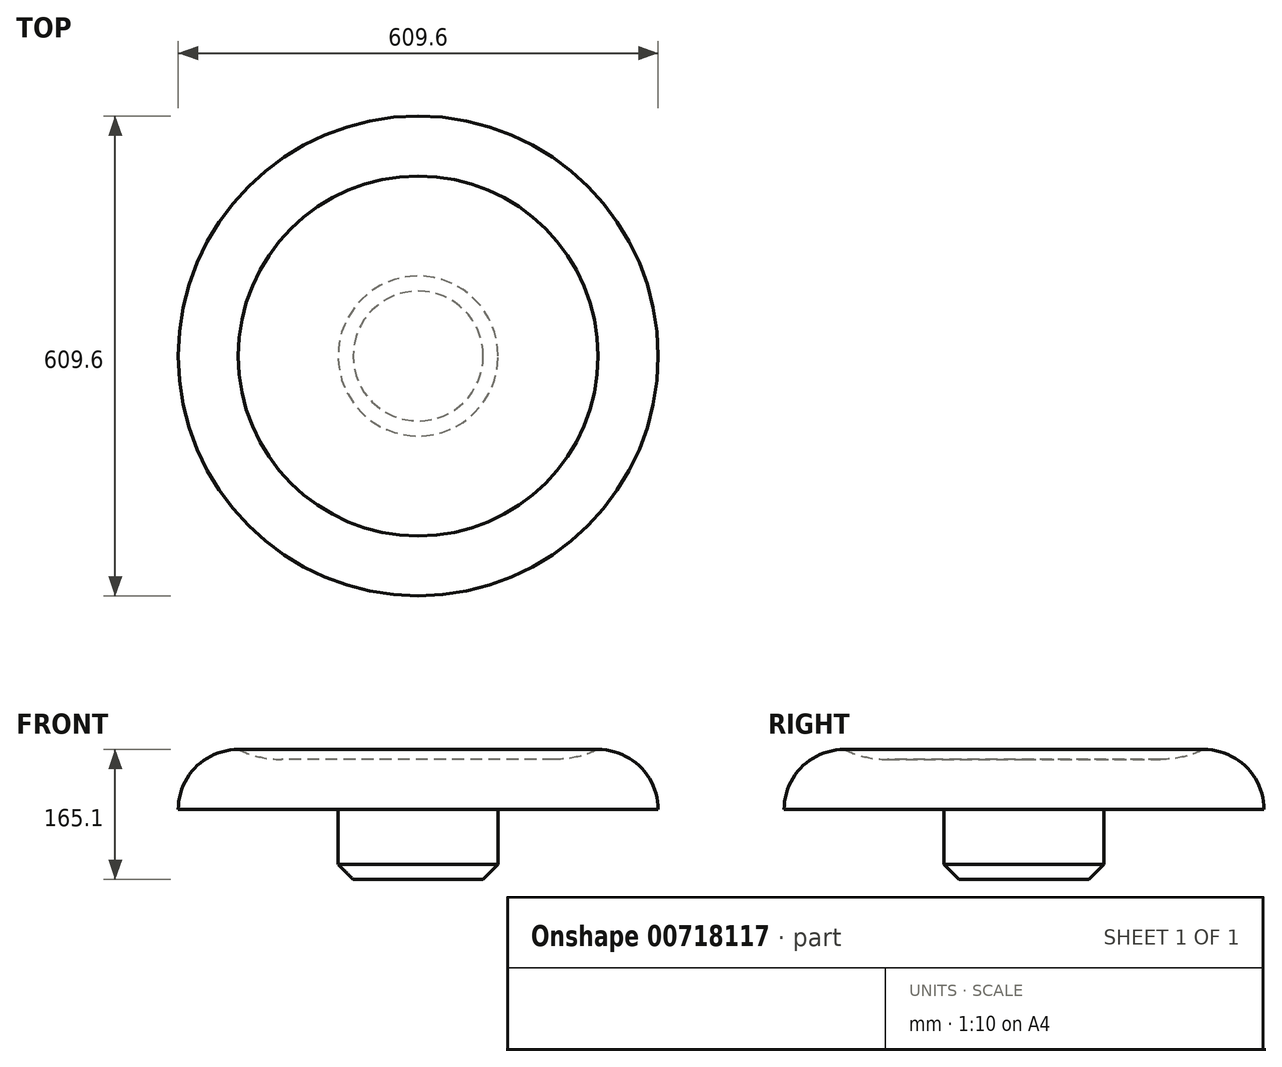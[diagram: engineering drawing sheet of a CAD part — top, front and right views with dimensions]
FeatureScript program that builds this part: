
annotation { "Feature Type Name" : "Feature", "Feature Type Description" : "" }
export const myFeature = defineFeature(function(context is Context, id is Id, definition is map)
    precondition{}
    {
        {
            var Q0;
            Q0=qCreatedBy(makeId("Top.planeOp"),FACE);
            var sketch = newSketch(context, id + "F0", { "sketchPlane" : qUnion([Q0])});
            skCircle(sketch, "E0", {"center": v(0, 0) * mm, "radius": 304.8 * mm});
            skSolve(sketch);
        }
        {
            var Q0;
            Q0=makeQuery(id+"F0.imprint","IMPRINT",FACE,{"disambiguationData":[TD([[makeQuery(id+"F0.imprint","IMPRINT",EDGE,{"derivedFrom":sQuery(id+"F0.wireOp",EDGE,"E0")}),1.0]])]});
            extrude(context, id + "F1", {"entities" : qUnion([Q0]), "depth" : 76.2 * mm, "offsetDistance" : 25.4 * mm});
        }
        {
            var Q0;
            Q0=makeQuery(id+"F1.opExtrude","CAP_FACE",FACE,{"disambiguationData":[OSD([sQuery(id+"F0.wireOp",EDGE,"E0")])],"isStart":true});
            var sketch = newSketch(context, id + "F2", { "sketchPlane" : qUnion([Q0])});
            skCircle(sketch, "E1", {"center": v(0, 0) * mm, "radius": 101.6 * mm});
            skSolve(sketch);
        }
        {
            var Q0;
            Q0=makeQuery(id+"F2.imprint","IMPRINT",FACE,{"disambiguationData":[TD([[makeQuery(id+"F2.imprint","IMPRINT",EDGE,{"derivedFrom":sQuery(id+"F2.wireOp",EDGE,"E1")}),1.0]])]});
            extrude(context, id + "F3", {"entities" : qUnion([Q0]), "operationType" : NewBodyOperationType.ADD, "depth" : 88.9 * mm, "offsetDistance" : 25.4 * mm});
        }
        {
            var Q0;
            Q0=makeQuery(id+"F3.opExtrude","CAP_EDGE",EDGE,{"disambiguationData":[OSD([sQuery(id+"F2.wireOp",EDGE,"E1")])],"isStart":false});
            chamfer(context, id + "F4", {"entities" : qUnion([Q0]), "width" : 19.05 * mm, "tangentPropagation" : true});
        }
        {
            var Q0;
            Q0=makeQuery(id+"F1.opExtrude","CAP_EDGE",EDGE,{"disambiguationData":[OSD([sQuery(id+"F0.wireOp",EDGE,"E0")])],"isStart":false});
            fillet(context, id + "F5", {"entities" : qUnion([Q0]), "radius" : 76.2 * mm, "tangentPropagation" : true, "allowEdgeOverflow" : false});
        }
        {
            var Q0;
            Q0=makeQuery(id+"F1.opExtrude","CAP_FACE",FACE,{"disambiguationData":[OSD([sQuery(id+"F0.wireOp",EDGE,"E0")])],"isStart":false});
            var sketch = newSketch(context, id + "F6", { "sketchPlane" : qUnion([Q0])});
            skCircle(sketch, "E2", {"center": v(0, 0) * mm, "radius": 228.6 * mm});
            skSolve(sketch);
        }
        {
            var Q0;
            Q0=makeQuery(id+"F6.imprint","IMPRINT",FACE,{"disambiguationData":[TD([[makeQuery(id+"F6.imprint","IMPRINT",EDGE,{"derivedFrom":sQuery(id+"F6.wireOp",EDGE,"E2")}),1.0]])]});
            extrude(context, id + "F7", {"entities" : qUnion([Q0]), "operationType" : NewBodyOperationType.REMOVE, "oppositeDirection" : true, "depth" : 12.7 * mm, "offsetDistance" : 25.4 * mm});
        }
        {
            var Q0;
            Q0=makeQuery(id+"F7.boolean.opBoolean","COPY",EDGE,{"derivedFrom":makeQuery(id+"F7.opExtrude","CAP_EDGE",EDGE,{"disambiguationData":[OSD([sQuery(id+"F6.wireOp",EDGE,"E2")])],"isStart":false})});
            fillet(context, id + "F8", {"entities" : qUnion([Q0]), "radius" : 127 * mm, "tangentPropagation" : true, "allowEdgeOverflow" : false});
        }
    });
